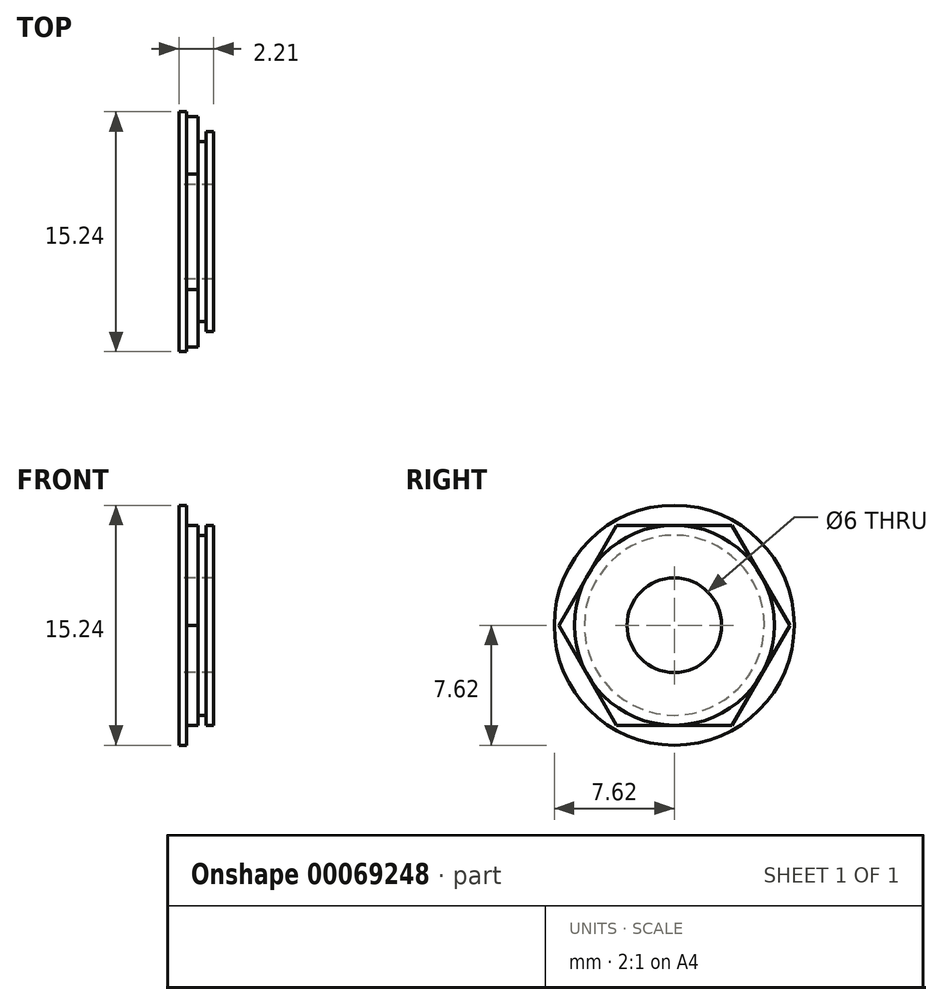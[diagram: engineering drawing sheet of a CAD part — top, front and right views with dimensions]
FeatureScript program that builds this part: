
annotation { "Feature Type Name" : "Feature", "Feature Type Description" : "" }
export const myFeature = defineFeature(function(context is Context, id is Id, definition is map)
    precondition{}
    {
        {
            assignVariable(context, id + "F0", {"name" : "shoulder_length", "anyValue" : .5});
        }
        {
            assignVariable(context, id + "F1", {"name" : "hex_length", "anyValue" : 0.71});
        }
        {
            var Q0;
            Q0=qCreatedBy(makeId("Right.planeOp"),FACE);
            var sketch = newSketch(context, id + "F2", { "sketchPlane" : qUnion([Q0])});
            skCircle(sketch, "E0", {"center": v(0, 0) * mm, "radius": 7.62 * mm});
            skCircle(sketch, "E1.cCircle", {"center": v(0, 0) * mm, "radius": 6.35 * mm});
            skLineSegment(sketch, "E1.0", {"start": v(-3.67, 6.35) * mm, "end": v(3.67, 6.35) * mm});
            skLineSegment(sketch, "E1.1", {"start": v(3.67, 6.35) * mm, "end": v(7.33, 0) * mm});
            skLineSegment(sketch, "E1.2", {"start": v(7.33, 0) * mm, "end": v(3.67, -6.35) * mm});
            skLineSegment(sketch, "E1.3", {"start": v(3.67, -6.35) * mm, "end": v(-3.67, -6.35) * mm});
            skLineSegment(sketch, "E1.4", {"start": v(-3.67, -6.35) * mm, "end": v(-7.33, 0) * mm});
            skLineSegment(sketch, "E1.5", {"start": v(-7.33, 0) * mm, "end": v(-3.67, 6.35) * mm});
            skPoint(sketch, "E1.0.midPoint", {"position": v(0, 6.35) * mm});
            skCircle(sketch, "E2.0", {"center": v(0, 0) * mm, "radius": 5.72 * mm});
            skCircle(sketch, "E3", {"center": v(0, 0) * mm, "radius": 3 * mm});
            skSolve(sketch);
        }
        {
            var Q0;
            Q0=makeQuery(id+"F2.imprint","IMPRINT",FACE,{"disambiguationData":[TD([[makeQuery(id+"F2.imprint","IMPRINT",EDGE,{"derivedFrom":sQuery(id+"F2.wireOp",EDGE,"E0")}),1.0]])]});
            extrude(context, id + "F3", {"entities" : qUnion([Q0]), "depth" : (getVariable(context, 'shoulder_length')) * mm});
        }
        {
            var Q0;
            {var subQ0=sQuery(id+"F2.wireOp",EDGE,"E1.0");var subQ1=sQuery(id+"F2.wireOp",EDGE,"E1.cCircle");var subQ2=makeQuery(id+"F2.imprint","INTERSECT",VERTEX,{"derivedFrom":[subQ1,subQ0]});Q0=makeQuery(id+"F2.imprint","IMPRINT",FACE,{"disambiguationData":[TD([[makeQuery(id+"F2.imprint","IMPRINT",EDGE,{"disambiguationData":[TD([[subQ2,-1.0]])],"derivedFrom":subQ1}),-1.0]])]});}
            var Q1;
            {var subQ0=sQuery(id+"F2.wireOp",EDGE,"E1.0");var subQ1=sQuery(id+"F2.wireOp",EDGE,"E1.cCircle");var subQ2=makeQuery(id+"F2.imprint","INTERSECT",VERTEX,{"derivedFrom":[subQ1,subQ0]});Q1=makeQuery(id+"F2.imprint","IMPRINT",FACE,{"disambiguationData":[TD([[makeQuery(id+"F2.imprint","IMPRINT",EDGE,{"disambiguationData":[TD([[subQ2,1.0]])],"derivedFrom":subQ1}),-1.0]])]});}
            var Q2;
            {var subQ0=sQuery(id+"F2.wireOp",EDGE,"E1.1");var subQ1=sQuery(id+"F2.wireOp",EDGE,"E1.cCircle");var subQ2=makeQuery(id+"F2.imprint","INTERSECT",VERTEX,{"derivedFrom":[subQ1,subQ0]});Q2=makeQuery(id+"F2.imprint","IMPRINT",FACE,{"disambiguationData":[TD([[makeQuery(id+"F2.imprint","IMPRINT",EDGE,{"disambiguationData":[TD([[subQ2,1.0]])],"derivedFrom":subQ1}),-1.0]])]});}
            var Q3;
            {var subQ0=sQuery(id+"F2.wireOp",EDGE,"E1.3");var subQ1=sQuery(id+"F2.wireOp",EDGE,"E1.cCircle");var subQ2=makeQuery(id+"F2.imprint","INTERSECT",VERTEX,{"derivedFrom":[subQ1,subQ0]});Q3=makeQuery(id+"F2.imprint","IMPRINT",FACE,{"disambiguationData":[TD([[makeQuery(id+"F2.imprint","IMPRINT",EDGE,{"disambiguationData":[TD([[subQ2,-1.0]])],"derivedFrom":subQ1}),-1.0]])]});}
            var Q4;
            {var subQ0=sQuery(id+"F2.wireOp",EDGE,"E1.4");var subQ1=sQuery(id+"F2.wireOp",EDGE,"E1.cCircle");var subQ2=makeQuery(id+"F2.imprint","INTERSECT",VERTEX,{"derivedFrom":[subQ1,subQ0]});Q4=makeQuery(id+"F2.imprint","IMPRINT",FACE,{"disambiguationData":[TD([[makeQuery(id+"F2.imprint","IMPRINT",EDGE,{"disambiguationData":[TD([[subQ2,-1.0]])],"derivedFrom":subQ1}),-1.0]])]});}
            var Q5;
            {var subQ0=sQuery(id+"F2.wireOp",EDGE,"E1.5");var subQ1=sQuery(id+"F2.wireOp",EDGE,"E1.cCircle");var subQ2=makeQuery(id+"F2.imprint","INTERSECT",VERTEX,{"derivedFrom":[subQ1,subQ0]});Q5=makeQuery(id+"F2.imprint","IMPRINT",FACE,{"disambiguationData":[TD([[makeQuery(id+"F2.imprint","IMPRINT",EDGE,{"disambiguationData":[TD([[subQ2,-1.0]])],"derivedFrom":subQ1}),-1.0]])]});}
            var Q6;
            Q6=makeQuery(id+"F2.imprint","IMPRINT",FACE,{"disambiguationData":[TD([[makeQuery(id+"F2.imprint","IMPRINT",EDGE,{"derivedFrom":sQuery(id+"F2.wireOp",EDGE,"E2.0")}),-1.0]])]});
            extrude(context, id + "F4", {"entities" : qUnion([Q0, Q1, Q2, Q3, Q4, Q5, Q6]), "operationType" : NewBodyOperationType.ADD, "depth" : (getVariable(context, 'shoulder_length') + getVariable(context, 'hex_length')) * mm});
        }
        {
            var Q0;
            Q0=makeQuery(id+"F2.imprint","IMPRINT",FACE,{"disambiguationData":[TD([[makeQuery(id+"F2.imprint","IMPRINT",EDGE,{"derivedFrom":sQuery(id+"F2.wireOp",EDGE,"E2.0")}),1.0]])]});
            extrude(context, id + "F5", {"entities" : qUnion([Q0]), "operationType" : NewBodyOperationType.ADD, "depth" : (getVariable(context, 'hex_length') + 3 * getVariable(context, 'shoulder_length')) * mm});
        }
        {
            var Q0;
            Q0=makeQuery(id+"F2.imprint","IMPRINT",FACE,{"disambiguationData":[TD([[makeQuery(id+"F2.imprint","IMPRINT",EDGE,{"derivedFrom":sQuery(id+"F2.wireOp",EDGE,"E2.0")}),-1.0]])]});
            var Q1;
            Q1=makeQuery(id+"F5.opExtrude","CAP_FACE",FACE,{"disambiguationData":[OSD([sQuery(id+"F2.wireOp",EDGE,"E2.0")])],"isStart":false});
            extrude(context, id + "F6", {"entities" : qUnion([Q0]), "operationType" : NewBodyOperationType.ADD, "endBound" : BoundingType.UP_TO_SURFACE, "endBoundEntityFace" : qUnion([Q1]), "depth" : 25.4 * mm, "hasSecondDirection" : true, "secondDirectionOppositeDirection" : false, "secondDirectionDepth" : (getVariable(context, 'shoulder_length') * 2 + getVariable(context, 'hex_length')) * mm});
        }
        {
            var Q0;
            Q0=qCreatedBy(makeId("Top.planeOp"),FACE);
            var sketch = newSketch(context, id + "F7", { "sketchPlane" : qUnion([Q0])});
            skLineSegment(sketch, "E4.0", {"start": v(21.84, 6.35) * mm, "end": v(21.84, -6.35) * mm, "construction": true});
            skLineSegment(sketch, "E5", {"start": v(0, 0) * mm, "end": v(21.84, 0) * mm, "construction": true});
            skCircle(sketch, "E6", {"center": v(5.08, 0) * mm, "radius": 1.27 * mm});
            skLineSegment(sketch, "E7.direction1", {"start": v(5.08, 0) * mm, "end": v(15.24, 0) * mm, "construction": true});
            skCircle(sketch, "E8.0.1.0", {"center": v(15.24, 0) * mm, "radius": 1.27 * mm});
            skSolve(sketch);
        }
        {
            var Q0;
            Q0=qSketchRegion(id+"F7",true);
            extrude(context, id + "F8", {"entities" : qUnion([Q0]), "operationType" : NewBodyOperationType.REMOVE, "endBound" : BoundingType.THROUGH_ALL, "depth" : 25.4 * mm});
        }
    });
